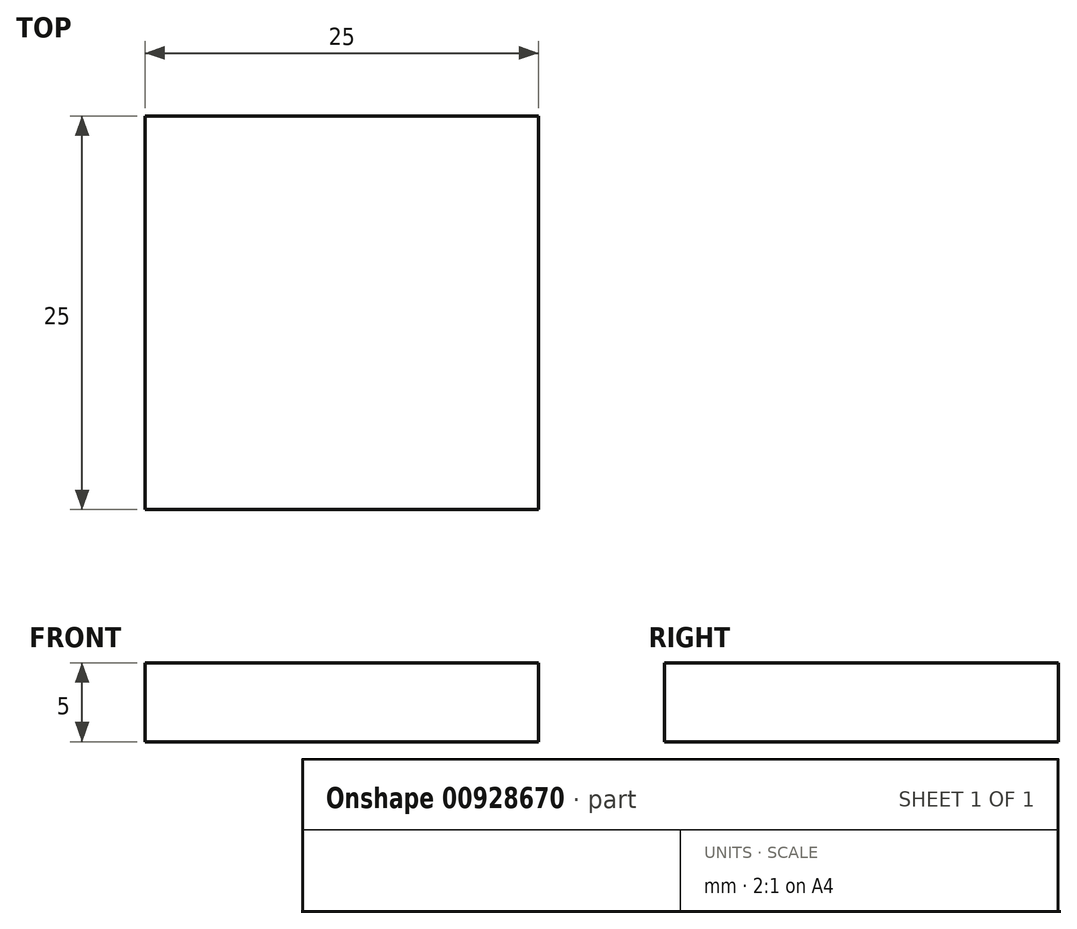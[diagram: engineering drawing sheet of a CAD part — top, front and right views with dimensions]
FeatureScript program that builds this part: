
annotation { "Feature Type Name" : "Feature", "Feature Type Description" : "" }
export const myFeature = defineFeature(function(context is Context, id is Id, definition is map)
    precondition{}
    {
        {
            var Q0;
            Q0=qCreatedBy(makeId("Top.planeOp"),FACE);
            var sketch = newSketch(context, id + "F0", { "sketchPlane" : qUnion([Q0])});
            skLineSegment(sketch, "E0.bottom", {"start": v(12.5, -12.5) * mm, "end": v(-12.5, -12.5) * mm});
            skLineSegment(sketch, "E0.top", {"start": v(12.5, 12.5) * mm, "end": v(-12.5, 12.5) * mm});
            skLineSegment(sketch, "E0.left", {"start": v(12.5, -12.5) * mm, "end": v(12.5, 12.5) * mm});
            skLineSegment(sketch, "E0.right", {"start": v(-12.5, -12.5) * mm, "end": v(-12.5, 12.5) * mm});
            skPoint(sketch, "E0.middle", {"position": v(0, 0) * mm});
            skSolve(sketch);
        }
        {
            var Q0;
            Q0=makeQuery(id+"F0.imprint","IMPRINT",FACE,{"disambiguationData":[TD([[makeQuery(id+"F0.imprint","IMPRINT",EDGE,{"derivedFrom":sQuery(id+"F0.wireOp",EDGE,"E0.bottom")}),-1.0]])]});
            extrude(context, id + "F1", {"entities" : qUnion([Q0]), "depth" : 5 * mm, "offsetDistance" : 25 * mm});
        }
    });
